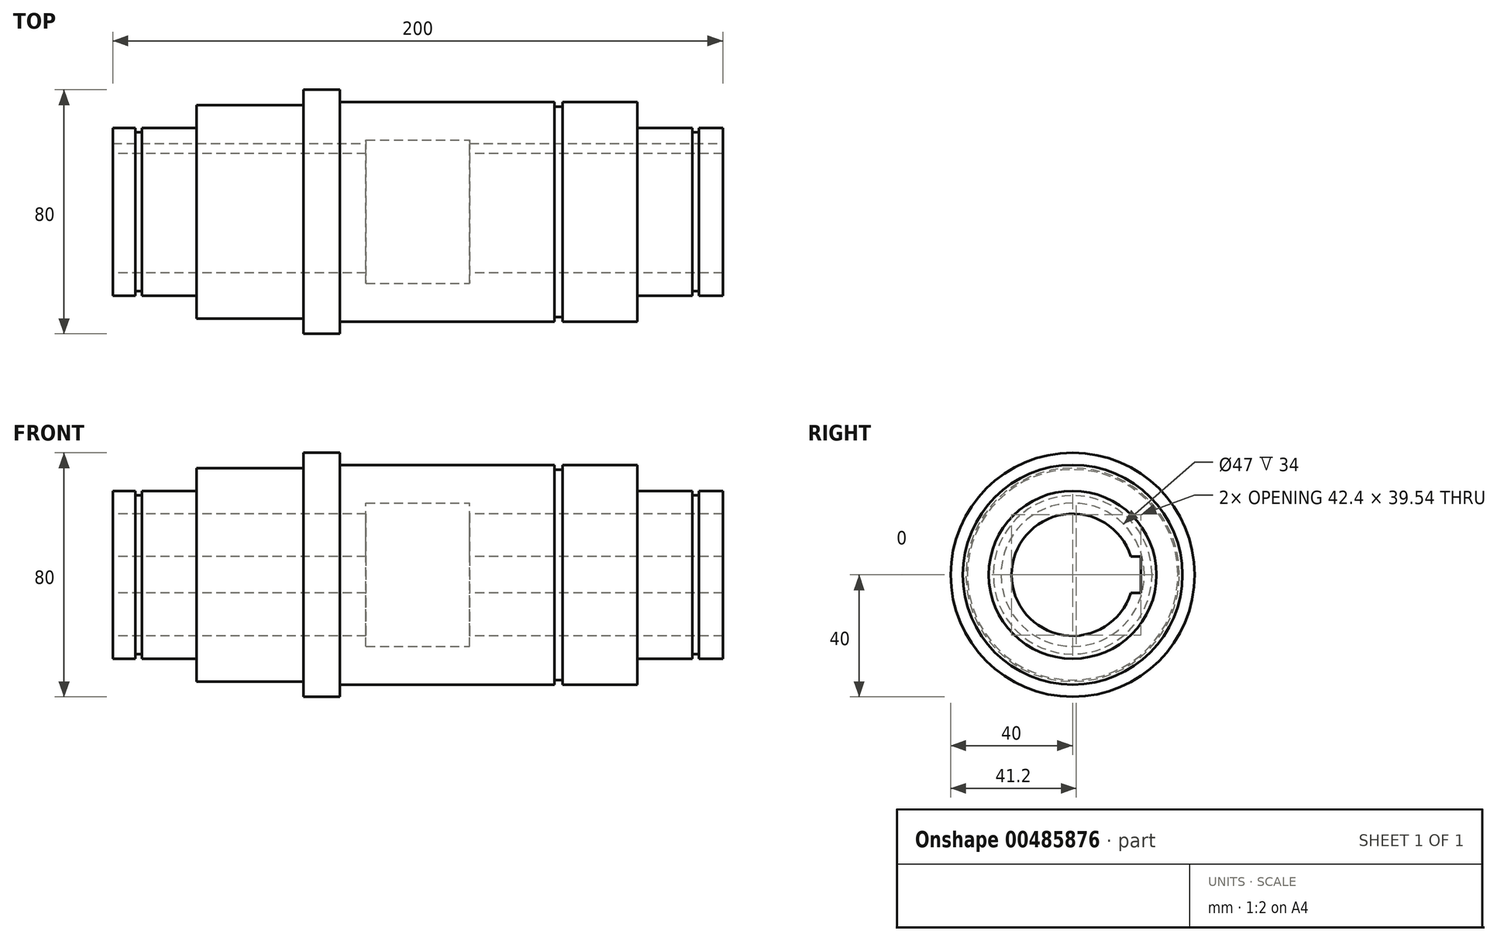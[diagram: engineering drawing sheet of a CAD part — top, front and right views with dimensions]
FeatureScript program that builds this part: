
annotation { "Feature Type Name" : "Feature", "Feature Type Description" : "" }
export const myFeature = defineFeature(function(context is Context, id is Id, definition is map)
    precondition{}
    {
        {
            var Q0;
            Q0=qCreatedBy(makeId("Front.planeOp"),FACE);
            var sketch = newSketch(context, id + "F0", { "sketchPlane" : qUnion([Q0])});
            skLineSegment(sketch, "E0", {"start": v(0, 20) * mm, "end": v(200, 20) * mm});
            skLineSegment(sketch, "E1", {"start": v(0, 20) * mm, "end": v(0, 27.5) * mm});
            skLineSegment(sketch, "E2", {"start": v(0, 27.5) * mm, "end": v(27.5, 27.5) * mm});
            skLineSegment(sketch, "E3", {"start": v(27.5, 27.5) * mm, "end": v(27.5, 35) * mm});
            skLineSegment(sketch, "E4", {"start": v(27.5, 35) * mm, "end": v(62.5, 35) * mm});
            skLineSegment(sketch, "E5", {"start": v(62.5, 35) * mm, "end": v(62.5, 40) * mm});
            skLineSegment(sketch, "E6", {"start": v(62.5, 40) * mm, "end": v(74.5, 40) * mm});
            skLineSegment(sketch, "E7", {"start": v(74.5, 40) * mm, "end": v(74.5, 36) * mm});
            skLineSegment(sketch, "E8", {"start": v(74.5, 36) * mm, "end": v(172, 36) * mm});
            skLineSegment(sketch, "E9", {"start": v(172, 36) * mm, "end": v(172, 27.5) * mm});
            skLineSegment(sketch, "E10", {"start": v(172, 27.5) * mm, "end": v(200, 27.5) * mm});
            skLineSegment(sketch, "E11", {"start": v(200, 27.5) * mm, "end": v(200, 20) * mm});
            skLineSegment(sketch, "E12", {"start": v(0, 0) * mm, "end": v(88.95, 0) * mm});
            skSolve(sketch);
        }
        {
            var Q0;
            Q0 = qSketchRegion(id + "F0", true);
            var Q1;
            Q1=sQuery(id+"F0.wireOp",EDGE,"E12");
            revolve(context, id + "F1", {"entities" : qUnion([Q0]), "axis" : qUnion([Q1]), "revolveType" : RevolveType.FULL});
        }
        {
            var Q0;
            Q0=qCreatedBy(makeId("Front.planeOp"),FACE);
            var sketch = newSketch(context, id + "F2", { "sketchPlane" : qUnion([Q0])});
            skLineSegment(sketch, "E13.bottom", {"start": v(83, 0) * mm, "end": v(117, 0) * mm});
            skLineSegment(sketch, "E13.top", {"start": v(83, 23.5) * mm, "end": v(117, 23.5) * mm});
            skLineSegment(sketch, "E13.left", {"start": v(83, 0) * mm, "end": v(83, 23.5) * mm});
            skLineSegment(sketch, "E13.right", {"start": v(117, 0) * mm, "end": v(117, 23.5) * mm});
            skSolve(sketch);
        }
        {
            var Q0;
            Q0 = qSketchRegion(id + "F2", true);
            var Q1;
            Q1=sQuery(id+"F2.wireOp",EDGE,"E13.bottom");
            revolve(context, id + "F3", {"operationType" : NewBodyOperationType.REMOVE, "entities" : qUnion([Q0]), "axis" : qUnion([Q1]), "revolveType" : RevolveType.FULL, "oppositeDirection" : true});
        }
        {
            var Q0;
            Q0=makeQuery(id+"F1.opRevolve","SWEPT_FACE",FACE,{"disambiguationData":[OSD([sQuery(id+"F0.wireOp",EDGE,"E11")])]});
            var sketch = newSketch(context, id + "F4", { "sketchPlane" : qUnion([Q0])});
            skLineSegment(sketch, "E14.bottom", {"start": v(12.4, 6) * mm, "end": v(22.4, 6) * mm});
            skLineSegment(sketch, "E14.top", {"start": v(12.4, -6) * mm, "end": v(22.4, -6) * mm});
            skLineSegment(sketch, "E14.left", {"start": v(12.4, 6) * mm, "end": v(12.4, -6) * mm});
            skLineSegment(sketch, "E14.right", {"start": v(22.4, 6) * mm, "end": v(22.4, -6) * mm});
            skSolve(sketch);
        }
        {
            var Q0;
            Q0 = qSketchRegion(id + "F4", true);
            extrude(context, id + "F5", {"entities" : qUnion([Q0]), "operationType" : NewBodyOperationType.REMOVE, "endBound" : BoundingType.THROUGH_ALL, "oppositeDirection" : true, "depth" : 25 * mm});
        }
        {
            var Q0;
            Q0=qCreatedBy(makeId("Front.planeOp"),FACE);
            var sketch = newSketch(context, id + "F6", { "sketchPlane" : qUnion([Q0])});
            skLineSegment(sketch, "E15.bottom", {"start": v(7.35, 36) * mm, "end": v(9.5, 36) * mm});
            skLineSegment(sketch, "E15.top", {"start": v(7.35, 26) * mm, "end": v(9.5, 26) * mm});
            skLineSegment(sketch, "E15.left", {"start": v(7.35, 36) * mm, "end": v(7.35, 26) * mm});
            skLineSegment(sketch, "E15.right", {"start": v(9.5, 36) * mm, "end": v(9.5, 26) * mm});
            skLineSegment(sketch, "E16.bottom", {"start": v(190, 36) * mm, "end": v(192.15, 36) * mm});
            skLineSegment(sketch, "E16.top", {"start": v(190, 26) * mm, "end": v(192.15, 26) * mm});
            skLineSegment(sketch, "E16.left", {"start": v(190, 36) * mm, "end": v(190, 26) * mm});
            skLineSegment(sketch, "E16.right", {"start": v(192.15, 36) * mm, "end": v(192.15, 26) * mm});
            skLineSegment(sketch, "E17.bottom", {"start": v(144.85, 44.5) * mm, "end": v(147.5, 44.5) * mm});
            skLineSegment(sketch, "E17.top", {"start": v(144.85, 34.5) * mm, "end": v(147.5, 34.5) * mm});
            skLineSegment(sketch, "E17.left", {"start": v(144.85, 44.5) * mm, "end": v(144.85, 34.5) * mm});
            skLineSegment(sketch, "E17.right", {"start": v(147.5, 44.5) * mm, "end": v(147.5, 34.5) * mm});
            skLineSegment(sketch, "E18", {"start": v(0, 0) * mm, "end": v(37.66, 0) * mm});
            skSolve(sketch);
        }
        {
            var Q0;
            Q0 = qSketchRegion(id + "F6", true);
            var Q1;
            Q1=sQuery(id+"F6.wireOp",EDGE,"E18");
            revolve(context, id + "F7", {"operationType" : NewBodyOperationType.REMOVE, "entities" : qUnion([Q0]), "axis" : qUnion([Q1]), "revolveType" : RevolveType.FULL});
        }
    });
